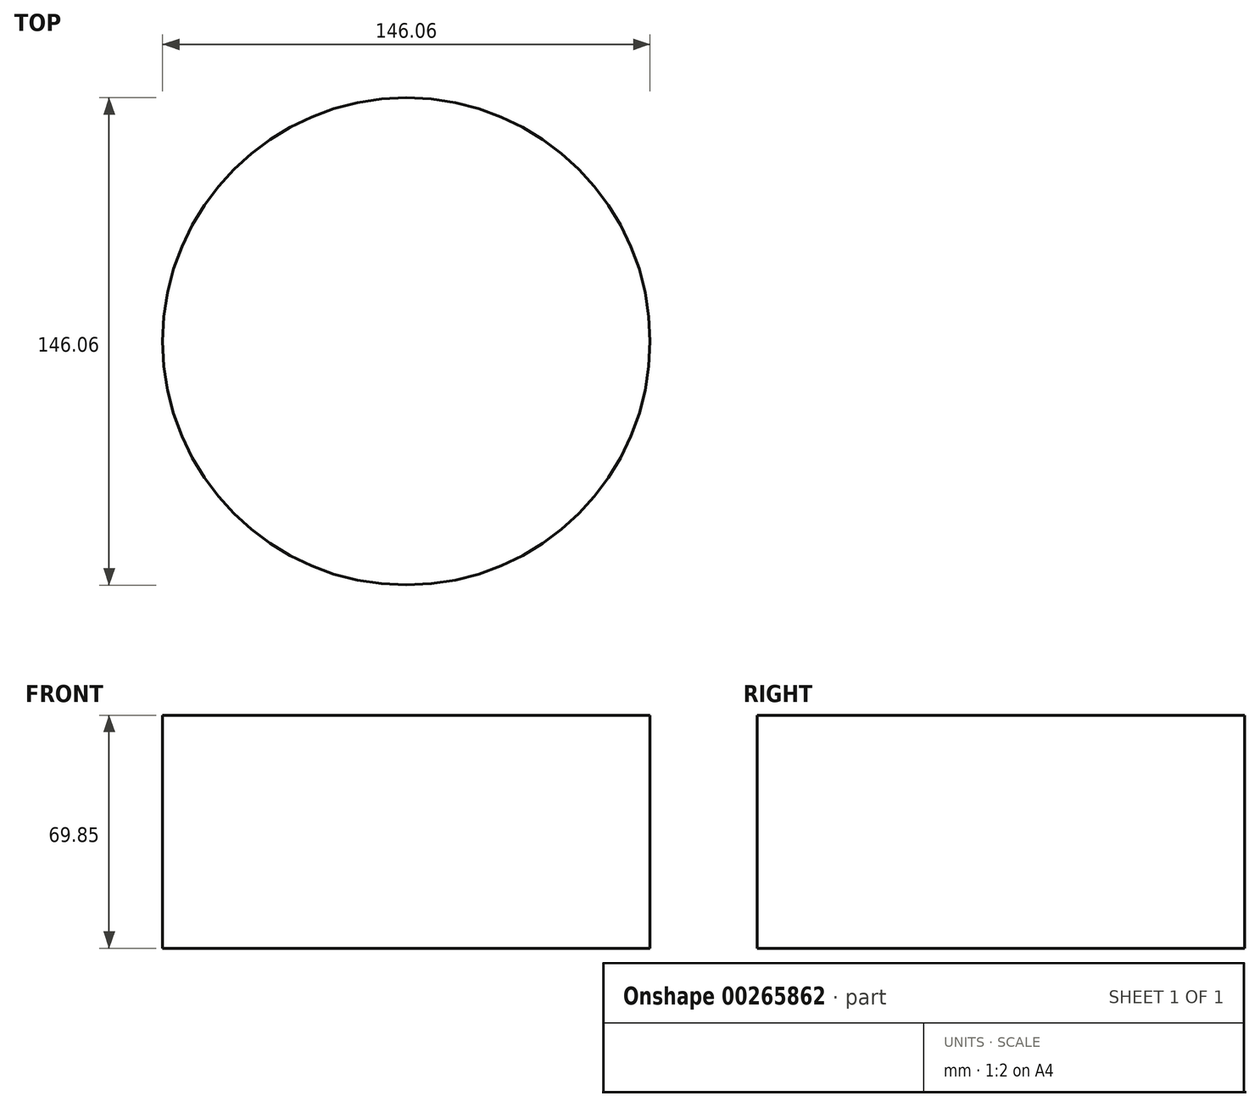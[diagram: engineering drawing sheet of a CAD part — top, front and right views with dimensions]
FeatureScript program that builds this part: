
annotation { "Feature Type Name" : "Feature", "Feature Type Description" : "" }
export const myFeature = defineFeature(function(context is Context, id is Id, definition is map)
    precondition{}
    {
        {
            var Q0;
            Q0=qCreatedBy(makeId("Top.planeOp"),FACE);
            var sketch = newSketch(context, id + "F0", { "sketchPlane" : qUnion([Q0])});
            skCircle(sketch, "E0", {"center": v(0, 0) * mm, "radius": 73.02 * mm});
            skSolve(sketch);
        }
        {
            var Q0;
            Q0 = qSketchRegion(id + "F0", true);
            extrude(context, id + "F1", {"entities" : qUnion([Q0]), "depth" : 69.85 * mm});
        }
        {
            var Q0;
            Q0=makeQuery(id+"F0.imprint","IMPRINT",FACE,{"disambiguationData":[TD([[makeQuery(id+"F0.imprint","IMPRINT",EDGE,{"derivedFrom":sQuery(id+"F0.wireOp",EDGE,"E0")}),1.0]])]});
            var sketch = newSketch(context, id + "F2", { "sketchPlane" : qUnion([Q0])});
            skLineSegment(sketch, "E1.bottom", {"start": v(-6.35, -60.96) * mm, "end": v(6.35, -60.96) * mm});
            skLineSegment(sketch, "E1.top", {"start": v(-6.35, 60.96) * mm, "end": v(6.35, 60.96) * mm});
            skLineSegment(sketch, "E1.left", {"start": v(-6.35, -60.96) * mm, "end": v(-6.35, 60.96) * mm});
            skLineSegment(sketch, "E1.right", {"start": v(6.35, -60.96) * mm, "end": v(6.35, 60.96) * mm});
            skPoint(sketch, "E1.middle", {"position": v(0, 0) * mm});
            skArc(sketch, "E2", {"start": v(-6.35, 60.96) * mm, "mid": v(-61.29, 0) * mm, "end": v(-6.35, -60.96) * mm});
            skArc(sketch, "E3", {"start": v(6.35, 60.96) * mm, "mid": v(61.29, 0) * mm, "end": v(6.35, -60.96) * mm});
            skSolve(sketch);
        }
        {
            var Q0;
            Q0=makeQuery(id+"F2.imprint","IMPRINT",FACE,{"disambiguationData":[TD([[makeQuery(id+"F2.imprint","IMPRINT",EDGE,{"derivedFrom":sQuery(id+"F2.wireOp",EDGE,"E1.left")}),1.0]])]});
            var Q1;
            Q1=makeQuery(id+"F2.imprint","IMPRINT",FACE,{"disambiguationData":[TD([[makeQuery(id+"F2.imprint","IMPRINT",EDGE,{"derivedFrom":sQuery(id+"F2.wireOp",EDGE,"E1.right")}),-1.0]])]});
            extrude(context, id + "F3", {"entities" : qUnion([Q0, Q1]), "operationType" : NewBodyOperationType.ADD, "depth" : 25.4 * mm});
        }
    });
